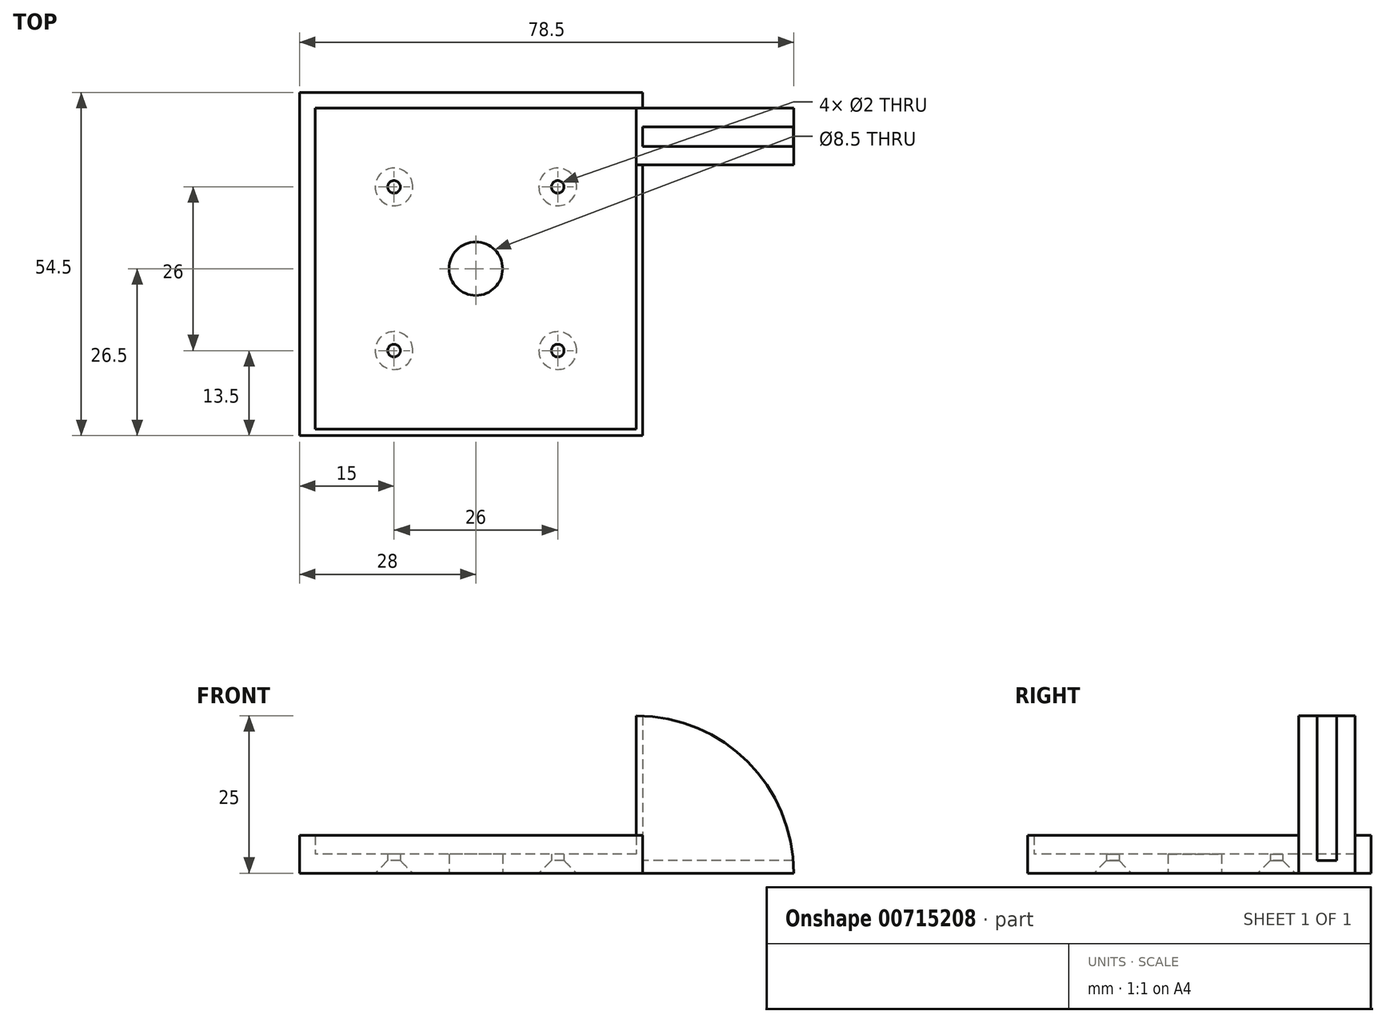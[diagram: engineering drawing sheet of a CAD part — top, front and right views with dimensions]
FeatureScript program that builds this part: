
annotation { "Feature Type Name" : "Feature", "Feature Type Description" : "" }
export const myFeature = defineFeature(function(context is Context, id is Id, definition is map)
    precondition{}
    {
        {
            var Q0;
            Q0=qCreatedBy(makeId("Top.planeOp"),FACE);
            var sketch = newSketch(context, id + "F0", { "sketchPlane" : qUnion([Q0])});
            skLineSegment(sketch, "E0.bottom", {"start": v(25.5, 25.5) * mm, "end": v(-25.5, 25.5) * mm});
            skLineSegment(sketch, "E0.top", {"start": v(25.5, -25.5) * mm, "end": v(-22.25, -25.5) * mm});
            skLineSegment(sketch, "E0.left", {"start": v(25.5, 25.5) * mm, "end": v(25.5, -25.5) * mm});
            skLineSegment(sketch, "E0.right", {"start": v(-25.5, 25.5) * mm, "end": v(-25.5, -25.5) * mm});
            skPoint(sketch, "E0.middle", {"position": v(0, 0) * mm});
            skLineSegment(sketch, "E1.0", {"start": v(28, 28) * mm, "end": v(-28, 28) * mm});
            skLineSegment(sketch, "E1.1", {"start": v(28, 28) * mm, "end": v(28, -28) * mm});
            skLineSegment(sketch, "E1.2", {"start": v(28, -28) * mm, "end": v(-22.25, -28) * mm});
            skLineSegment(sketch, "E1.3", {"start": v(-28, 28) * mm, "end": v(-28, -28) * mm});
            skCircle(sketch, "E2", {"center": v(-13, 13) * mm, "radius": 1 * mm});
            skLineSegment(sketch, "E3", {"start": v(0, 28) * mm, "end": v(0, -28) * mm, "construction": true});
            skLineSegment(sketch, "E4", {"start": v(-28, 0) * mm, "end": v(28, 0) * mm, "construction": true});
            skCircle(sketch, "E5.MirrorC", {"center": v(13, 13) * mm, "radius": 1 * mm});
            skCircle(sketch, "E6.MirrorC", {"center": v(13, -13) * mm, "radius": 1 * mm});
            skCircle(sketch, "E7.MirrorC", {"center": v(-13, -13) * mm, "radius": 1 * mm});
            skLineSegment(sketch, "E8.1", {"start": v(28, 30) * mm, "end": v(-30, 30) * mm});
            skLineSegment(sketch, "E9", {"start": v(28, 30) * mm, "end": v(28, 28) * mm});
            skLineSegment(sketch, "E10", {"start": v(-28, -28) * mm, "end": v(-30, -28) * mm});
            skLineSegment(sketch, "E11", {"start": v(28, 23.2) * mm, "end": v(28, 12.96) * mm});
            skLineSegment(sketch, "E12", {"start": v(28, 23.2) * mm, "end": v(28, 20) * mm});
            skLineSegment(sketch, "E13.trimOffspring", {"start": v(-25.25, -28) * mm, "end": v(-28, -28) * mm});
            skLineSegment(sketch, "E14", {"start": v(-25.5, -25.5) * mm, "end": v(-22.25, -25.5) * mm});
            skLineSegment(sketch, "E15", {"start": v(-25.25, -28) * mm, "end": v(-22.25, -28) * mm});
            skCircle(sketch, "E16", {"center": v(0, 0) * mm, "radius": 4.25 * mm});
            skLineSegment(sketch, "E17", {"start": v(-30, 30) * mm, "end": v(-30, -28) * mm});
            skSolve(sketch);
        }
        {
            var Q0;
            Q0=qCreatedBy(makeId("Top.planeOp"),FACE);
            var sketch = newSketch(context, id + "F1", { "sketchPlane" : qUnion([Q0])});
            skPoint(sketch, "E18.0", {"position": v(-25.5, -25.5) * mm});
            skLineSegment(sketch, "E19.bottom", {"start": v(-25.5, -25.5) * mm, "end": v(-16.5, -25.5) * mm});
            skLineSegment(sketch, "E19.top", {"start": v(-25.5, -50.5) * mm, "end": v(-16.5, -50.5) * mm});
            skLineSegment(sketch, "E19.left", {"start": v(-25.5, -25.5) * mm, "end": v(-25.5, -50.5) * mm});
            skLineSegment(sketch, "E19.right", {"start": v(-16.5, -25.5) * mm, "end": v(-16.5, -50.5) * mm});
            skLineSegment(sketch, "E20", {"start": v(-21, -50.5) * mm, "end": v(-21, -25.5) * mm, "construction": true});
            skLineSegment(sketch, "E21", {"start": v(-19.45, -25.5) * mm, "end": v(-19.45, -50.5) * mm});
            skLineSegment(sketch, "E22.MirrorCS", {"start": v(-22.55, -25.5) * mm, "end": v(-22.55, -50.5) * mm});
            skPoint(sketch, "E23.0", {"position": v(25.5, 25.5) * mm});
            skLineSegment(sketch, "E24.bottom", {"start": v(25.5, 25.5) * mm, "end": v(50.5, 25.5) * mm});
            skLineSegment(sketch, "E24.top", {"start": v(25.5, 16.5) * mm, "end": v(50.5, 16.5) * mm});
            skLineSegment(sketch, "E24.left", {"start": v(25.5, 25.5) * mm, "end": v(25.5, 16.5) * mm});
            skLineSegment(sketch, "E24.right", {"start": v(50.5, 25.5) * mm, "end": v(50.5, 16.5) * mm});
            skLineSegment(sketch, "E25", {"start": v(25.5, 21) * mm, "end": v(50.5, 21) * mm, "construction": true});
            skLineSegment(sketch, "E26", {"start": v(50.5, 22.55) * mm, "end": v(25.5, 22.55) * mm});
            skLineSegment(sketch, "E27.MirrorCS", {"start": v(50.5, 19.45) * mm, "end": v(25.5, 19.45) * mm});
            skSolve(sketch);
        }
        {
            var Q0;
            Q0=makeQuery(id+"F0.imprint","IMPRINT",FACE,{"disambiguationData":[TD([[makeQuery(id+"F0.imprint","IMPRINT",EDGE,{"derivedFrom":sQuery(id+"F0.wireOp",EDGE,"E0.bottom")}),1.0]])]});
            extrude(context, id + "F2", {"entities" : qUnion([Q0]), "depth" : 3 * mm, "offsetDistance" : 25 * mm});
        }
        {
            var Q0;
            Q0=makeQuery(id+"F0.imprint","IMPRINT",FACE,{"disambiguationData":[TD([[makeQuery(id+"F0.imprint","IMPRINT",EDGE,{"derivedFrom":sQuery(id+"F0.wireOp",EDGE,"E0.bottom")}),-1.0]])]});
            var Q1;
            {var subQ5=sQuery(id+"F0.wireOp",EDGE,"TI18WCdd-EPFC-hNpH-Rctt-afuqL8Zf6Xfq");Q1=makeQuery(id+"F0.imprint","IMPRINT",FACE,{"disambiguationData":[TD([[makeQuery(id+"F0.imprint","IMPRINT",EDGE,{"derivedFrom":subQ5}),-1.0]])]});}
            extrude(context, id + "F3", {"entities" : qUnion([Q0, Q1]), "operationType" : NewBodyOperationType.ADD, "depth" : 6 * mm, "offsetDistance" : 25 * mm});
        }
        {
            var Q0;
            Q0=makeQuery(id+"F2.opExtrude","CAP_EDGE",EDGE,{"disambiguationData":[OSD([sQuery(id+"F0.wireOp",EDGE,"E7.MirrorC")])],"isStart":true});
            var Q1;
            Q1=makeQuery(id+"F2.opExtrude","CAP_EDGE",EDGE,{"disambiguationData":[OSD([sQuery(id+"F0.wireOp",EDGE,"E6.MirrorC")])],"isStart":true});
            var Q2;
            Q2=makeQuery(id+"F2.opExtrude","CAP_EDGE",EDGE,{"disambiguationData":[OSD([sQuery(id+"F0.wireOp",EDGE,"E5.MirrorC")])],"isStart":true});
            var Q3;
            Q3=makeQuery(id+"F2.opExtrude","CAP_EDGE",EDGE,{"disambiguationData":[OSD([sQuery(id+"F0.wireOp",EDGE,"E2")])],"isStart":true});
            chamfer(context, id + "F4", {"entities" : qUnion([Q0, Q1, Q2, Q3]), "width" : 2 * mm, "tangentPropagation" : true});
        }
        {
            var Q0;
            Q0=makeQuery(id+"FIbiUBh41szAzK7_1.boolean.opBoolean","MERGE",FACE,{"derivedFrom":[makeQuery(id+"F3.opExtrude","SWEPT_FACE",FACE,{"disambiguationData":[OSD([sQuery(id+"F0.wireOp",EDGE,"E1.2"),sQuery(id+"F0.wireOp",EDGE,"E13.trimOffspring"),sQuery(id+"F0.wireOp",EDGE,"E15")])]}),makeQuery(id+"FIbiUBh41szAzK7_1.opExtrude","SWEPT_FACE",FACE,{"disambiguationData":[OSD([sQuery(id+"F0.wireOp",EDGE,"E10")])]})]});
            extrude(context, id + "F5", {"entities" : qUnion([Q0]), "operationType" : NewBodyOperationType.REMOVE, "oppositeDirection" : true, "depth" : 1.5 * mm, "offsetDistance" : 25 * mm});
        }
        {
            var Q0;
            Q0=makeQuery(id+"FIbiUBh41szAzK7_1.boolean.opBoolean","MERGE",FACE,{"derivedFrom":[makeQuery(id+"F3.opExtrude","SWEPT_FACE",FACE,{"disambiguationData":[OSD([sQuery(id+"F0.wireOp",EDGE,"E1.1"),sQuery(id+"F0.wireOp",EDGE,"E11"),sQuery(id+"F0.wireOp",EDGE,"E12")])]}),makeQuery(id+"FIbiUBh41szAzK7_1.opExtrude","SWEPT_FACE",FACE,{"disambiguationData":[OSD([sQuery(id+"F0.wireOp",EDGE,"E9")])]})]});
            extrude(context, id + "F6", {"entities" : qUnion([Q0]), "operationType" : NewBodyOperationType.REMOVE, "oppositeDirection" : true, "depth" : 1.5 * mm, "offsetDistance" : 25 * mm});
        }
        {
            var Q0;
            {var subQ0=sQuery(id+"F1.wireOp",EDGE,"E24.top");Q0=makeQuery(id+"F1.imprint","IMPRINT",FACE,{"disambiguationData":[TD([[makeQuery(id+"F1.imprint","IMPRINT",EDGE,{"derivedFrom":subQ0}),1.0]])]});}
            var Q1;
            {var subQ0=sQuery(id+"F1.wireOp",EDGE,"E24.bottom");Q1=makeQuery(id+"F1.imprint","IMPRINT",FACE,{"disambiguationData":[TD([[makeQuery(id+"F1.imprint","IMPRINT",EDGE,{"derivedFrom":subQ0}),-1.0]])]});}
            extrude(context, id + "F7", {"entities" : qUnion([Q0, Q1]), "operationType" : NewBodyOperationType.ADD, "depth" : 25 * mm, "offsetDistance" : 25 * mm});
        }
        {
            var Q0;
            {var subQ0=sQuery(id+"F1.wireOp",EDGE,"E26");Q0=makeQuery(id+"F1.imprint","IMPRINT",FACE,{"disambiguationData":[TD([[makeQuery(id+"F1.imprint","IMPRINT",EDGE,{"derivedFrom":subQ0}),1.0]])]});}
            extrude(context, id + "F8", {"entities" : qUnion([Q0]), "operationType" : NewBodyOperationType.ADD, "depth" : 2 * mm, "offsetDistance" : 25 * mm});
        }
        {
            var Q0;
            {var subQ1=sQuery(id+"F1.wireOp",EDGE,"E26");var subQ2=sQuery(id+"F0.wireOp",EDGE,"E12");var subQ3=sQuery(id+"F0.wireOp",EDGE,"E11");var subQ4=sQuery(id+"F0.wireOp",EDGE,"E1.1");var subQ6=sQuery(id+"F0.wireOp",EDGE,"E0.left");Q0=makeQuery(id+"F7.boolean.opBoolean","SPLIT",FACE,{"disambiguationData":[TD([makeQuery(id+"F7.opExtrude","SWEPT_FACE",FACE,{"disambiguationData":[OSD([subQ1])]})])],"derivedFrom":makeQuery(id+"F3.opExtrude","CAP_FACE",FACE,{"disambiguationData":[OSD([sQuery(id+"F0.wireOp",EDGE,"E0.bottom"),sQuery(id+"F0.wireOp",EDGE,"E0.top"),subQ6,sQuery(id+"F0.wireOp",EDGE,"E0.right"),sQuery(id+"F0.wireOp",EDGE,"E1.0"),subQ4,sQuery(id+"F0.wireOp",EDGE,"E1.2"),sQuery(id+"F0.wireOp",EDGE,"E1.3"),subQ3,subQ2,sQuery(id+"F0.wireOp",EDGE,"E13.trimOffspring"),sQuery(id+"F0.wireOp",EDGE,"E14"),sQuery(id+"F0.wireOp",EDGE,"E15")])],"isStart":false})});}
            var Q1;
            Q1=makeQuery(id+"F7.opExtrude","CAP_FACE",FACE,{"disambiguationData":[OSD([sQuery(id+"F1.wireOp",EDGE,"E24.top"),sQuery(id+"F1.wireOp",EDGE,"E24.left"),sQuery(id+"F1.wireOp",EDGE,"E24.right"),sQuery(id+"F1.wireOp",EDGE,"E27.MirrorCS")])],"isStart":false});
            var Q2;
            Q2=makeQuery(id+"F2.opExtrude","SWEPT_BODY",BODY,{"disambiguationData":[OSD([sQuery(id+"F0.wireOp",EDGE,"E0.bottom"),sQuery(id+"F0.wireOp",EDGE,"E0.top"),sQuery(id+"F0.wireOp",EDGE,"E0.left"),sQuery(id+"F0.wireOp",EDGE,"E0.right"),sQuery(id+"F0.wireOp",EDGE,"E2"),sQuery(id+"F0.wireOp",EDGE,"E5.MirrorC"),sQuery(id+"F0.wireOp",EDGE,"E6.MirrorC"),sQuery(id+"F0.wireOp",EDGE,"E7.MirrorC"),sQuery(id+"F0.wireOp",EDGE,"E14"),sQuery(id+"F0.wireOp",EDGE,"E16")])]});
            extrude(context, id + "F9", {"entities" : qUnion([Q0]), "operationType" : NewBodyOperationType.ADD, "endBound" : BoundingType.UP_TO_SURFACE, "depth" : 25 * mm, "endBoundEntityFace" : qUnion([Q1]), "endBoundEntityBody" : qUnion([Q2]), "offsetDistance" : 25 * mm});
        }
        {
            var Q0;
            {var subQ0=sQuery(id+"F1.wireOp",EDGE,"E19.top");Q0=makeQuery(id+"F7.opExtrude","CAP_EDGE",EDGE,{"disambiguationData":[OSD([subQ0]),TDD([makeQuery(id+"F1.imprint","IMPRINT",EDGE,{"disambiguationData":[TD([[makeQuery(id+"F1.imprint","INTERSECT",VERTEX,{"derivedFrom":[subQ0,sQuery(id+"F1.wireOp",EDGE,"E19.left")]}),-1.0]])],"derivedFrom":subQ0})])],"isStart":false});}
            var Q1;
            {var subQ0=sQuery(id+"F1.wireOp",EDGE,"E19.top");Q1=makeQuery(id+"F7.opExtrude","CAP_EDGE",EDGE,{"disambiguationData":[OSD([subQ0]),TDD([makeQuery(id+"F1.imprint","IMPRINT",EDGE,{"disambiguationData":[TD([[makeQuery(id+"F1.imprint","INTERSECT",VERTEX,{"derivedFrom":[subQ0,sQuery(id+"F1.wireOp",EDGE,"E19.right")]}),1.0]])],"derivedFrom":subQ0})])],"isStart":false});}
            var Q2;
            {var subQ0=sQuery(id+"F1.wireOp",EDGE,"E24.right");Q2=makeQuery(id+"F7.opExtrude","CAP_EDGE",EDGE,{"disambiguationData":[OSD([subQ0]),TDD([makeQuery(id+"F1.imprint","IMPRINT",EDGE,{"disambiguationData":[TD([[makeQuery(id+"F1.imprint","INTERSECT",VERTEX,{"derivedFrom":[sQuery(id+"F1.wireOp",EDGE,"E24.bottom"),subQ0]}),-1.0]])],"derivedFrom":subQ0})])],"isStart":false});}
            fillet(context, id + "F10", {"entities" : qUnion([Q0, Q1, Q2]), "radius" : 25 * mm, "tangentPropagation" : true, "allowEdgeOverflow" : false});
        }
    });
